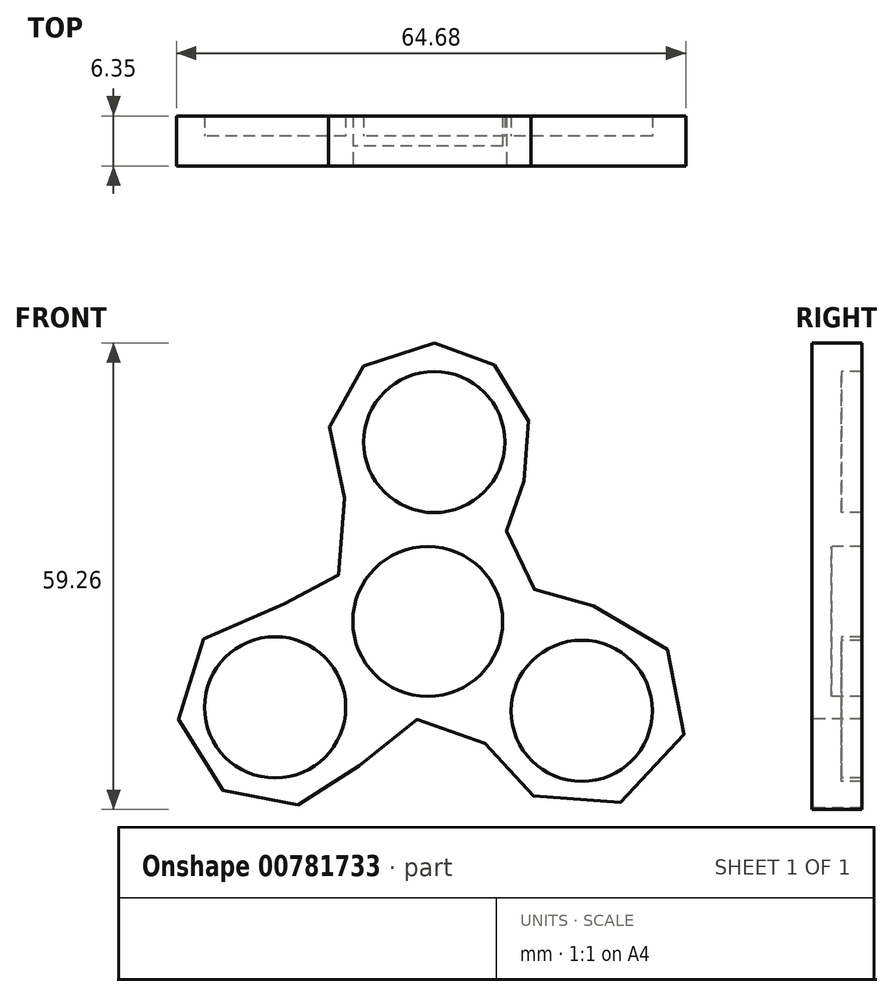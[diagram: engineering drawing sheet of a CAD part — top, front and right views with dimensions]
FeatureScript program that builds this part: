
annotation { "Feature Type Name" : "Feature", "Feature Type Description" : "" }
export const myFeature = defineFeature(function(context is Context, id is Id, definition is map)
    precondition{}
    {
        {
            var Q0;
            Q0=qCreatedBy(makeId("Front.planeOp"),FACE);
            var sketch = newSketch(context, id + "F0", { "sketchPlane" : qUnion([Q0])});
            skFitSpline(sketch, "E0", {"points": [v(0, 34.46) * mm, v(2.95, 34.15) * mm, v(5.19, 33.19) * mm, v(7.71, 31.6) * mm, v(9.49, 29.91) * mm, v(11.53, 26.27) * mm, v(12, 24.37) * mm, v(12.31, 21.8) * mm, v(12, 19.16) * mm, v(11.4, 16.95) * mm, v(10.8, 15.8) * mm, v(9.85, 13.8) * mm, v(9.35, 12.22) * mm, v(9.22, 9.8) * mm, v(9.85, 7.12) * mm, v(11.7, 4.08) * mm, v(13.47, 2.62) * mm, v(15.8, 1.44) * mm, v(18.28, 1.09) * mm, v(21.63, 0.89) * mm, v(26.31, -1.16) * mm, v(30.03, -5.2) * mm, v(31.18, -8.98) * mm, v(31.8, -14.94) * mm, v(27.98, -21.16) * mm, v(24.07, -23.72) * mm, v(18.24, -24.8) * mm, v(13.37, -23.51) * mm, v(10.17, -21.27) * mm, v(7.73, -18.58) * mm, v(6.26, -16.14) * mm, v(3.12, -14.15) * mm, v(-0.66, -13.32) * mm, v(-3.93, -13.77) * mm, v(-7.2, -16.01) * mm, v(-9.64, -19.35) * mm, v(-12.26, -21.84) * mm, v(-14.7, -23.25) * mm, v(-19.25, -24.54) * mm, v(-23.35, -24.02) * mm, v(-26.56, -22.55) * mm, v(-29.76, -19.8) * mm, v(-32, -15.37) * mm, v(-32.59, -9.15) * mm, v(-30.6, -4.99) * mm, v(-27.65, -1.4) * mm, v(-21.75, 1.16) * mm, v(-18.16, 1.36) * mm, v(-15.95, 1.96) * mm, v(-13.32, 3.69) * mm, v(-11.64, 5.87) * mm, v(-10.3, 10.09) * mm, v(-11.33, 14.61) * mm, v(-12.63, 17.3) * mm, v(-13.33, 20) * mm, v(-13.14, 24.9) * mm, v(-12.32, 26.93) * mm, v(-10.3, 30.34) * mm, v(-7.33, 32.65) * mm, v(-4.6, 33.96) * mm, v(0, 34.46) * mm]});
            skCircle(sketch, "E1", {"center": v(0, 21.89) * mm, "radius": 8.97 * mm});
            skCircle(sketch, "E2", {"center": v(18.73, -12.26) * mm, "radius": 8.97 * mm});
            skCircle(sketch, "E3", {"center": v(-20.21, -11.81) * mm, "radius": 8.97 * mm});
            skCircle(sketch, "E4", {"center": v(-0.82, -0.9) * mm, "radius": 9.52 * mm});
            skSolve(sketch);
        }
        {
            var Q0;
            Q0=sQuery(id+"F0.wireOp",EDGE,"E0");
            extrude(context, id + "F1", {"bodyType" : ToolBodyType.SURFACE, "surfaceEntities" : qUnion([Q0]), "depth" : 6.35 * mm, "offsetDistance" : 25.4 * mm});
        }
        {
            var Q0;
            Q0=sQuery(id+"F0.wireOp",EDGE,"E1");
            var Q1;
            Q1=sQuery(id+"F0.wireOp",EDGE,"E3");
            var Q2;
            Q2=sQuery(id+"F0.wireOp",EDGE,"E2");
            extrude(context, id + "F2", {"bodyType" : ToolBodyType.SURFACE, "surfaceEntities" : qUnion([Q0, Q1, Q2]), "depth" : 2.54 * mm, "offsetDistance" : 25.4 * mm});
        }
        {
            var Q0;
            Q0=sQuery(id+"F0.wireOp",EDGE,"E4");
            extrude(context, id + "F3", {"bodyType" : ToolBodyType.SURFACE, "surfaceEntities" : qUnion([Q0]), "depth" : 3.8 * mm, "offsetDistance" : 25.4 * mm});
        }
    });
